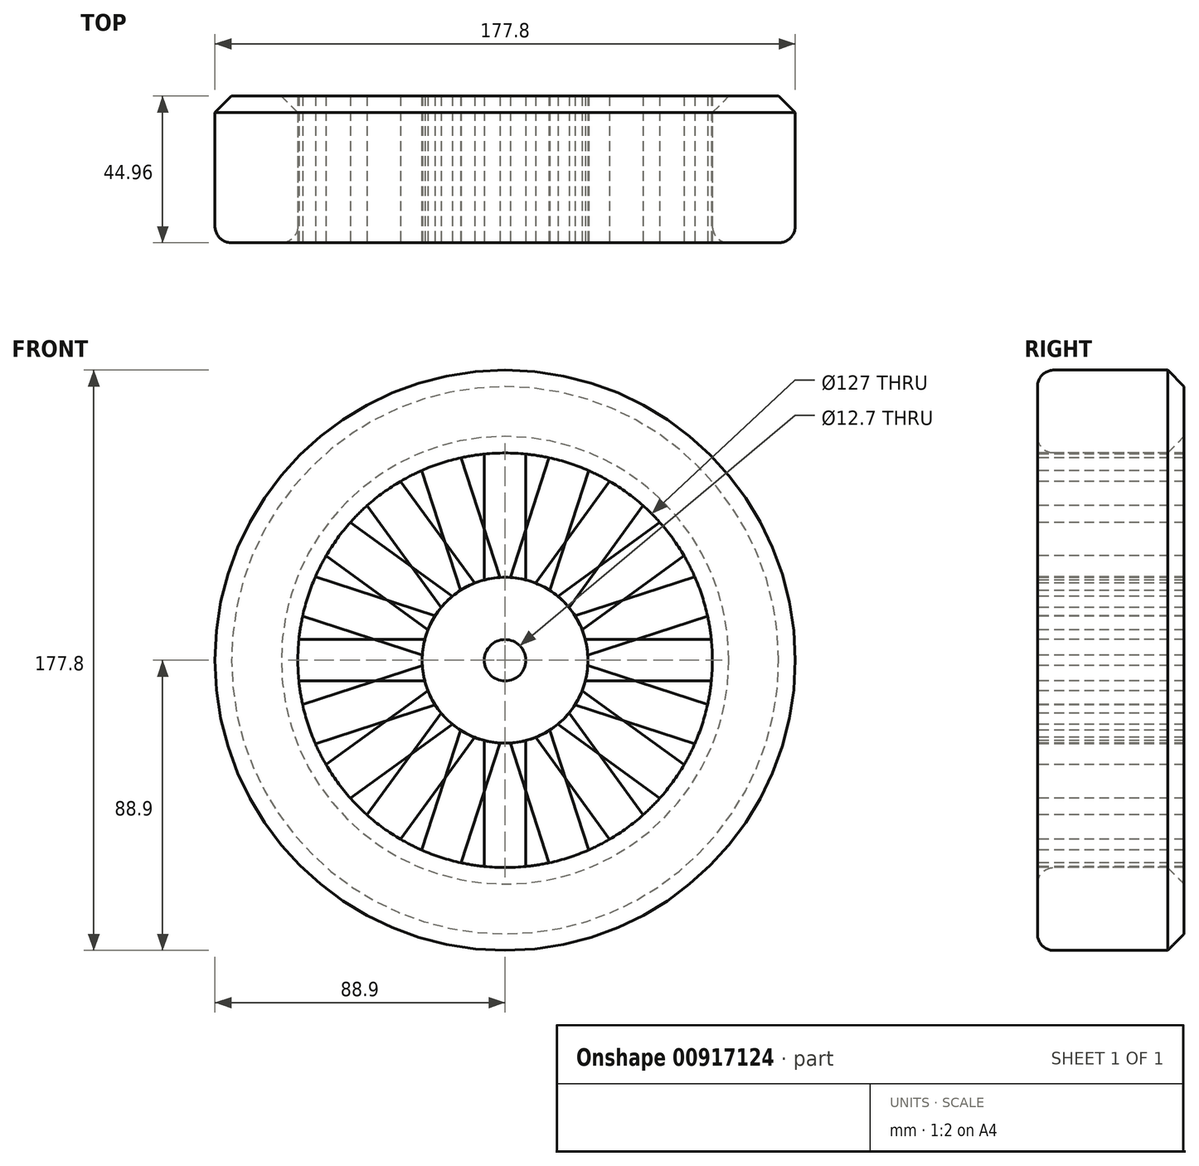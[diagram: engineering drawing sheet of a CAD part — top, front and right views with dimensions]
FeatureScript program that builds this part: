
annotation { "Feature Type Name" : "Feature", "Feature Type Description" : "" }
export const myFeature = defineFeature(function(context is Context, id is Id, definition is map)
    precondition{}
    {
        {
            var Q0;
            Q0=qCreatedBy(makeId("Front.planeOp"),FACE);
            var sketch = newSketch(context, id + "F0", { "sketchPlane" : qUnion([Q0])});
            skCircle(sketch, "E0", {"center": v(0, 0) * mm, "radius": 88.9 * mm});
            skSolve(sketch);
        }
        {
            var Q0;
            Q0=makeQuery(id+"F0.imprint","IMPRINT",FACE,{"disambiguationData":[TD([[makeQuery(id+"F0.imprint","IMPRINT",EDGE,{"derivedFrom":sQuery(id+"F0.wireOp",EDGE,"E0")}),1.0]])]});
            extrude(context, id + "F1", {"entities" : qUnion([Q0]), "depth" : 44.96 * mm, "offsetDistance" : 25.4 * mm});
        }
        {
            var Q0;
            Q0=makeQuery(id+"F1.opExtrude","CAP_FACE",FACE,{"disambiguationData":[OSD([sQuery(id+"F0.wireOp",EDGE,"E0")])],"isStart":false});
            var sketch = newSketch(context, id + "F2", { "sketchPlane" : qUnion([Q0])});
            skCircle(sketch, "E1", {"center": v(0, 0) * mm, "radius": 63.5 * mm});
            skSolve(sketch);
        }
        {
            var Q0;
            Q0=makeQuery(id+"F2.imprint","IMPRINT",FACE,{"disambiguationData":[TD([[makeQuery(id+"F2.imprint","IMPRINT",EDGE,{"derivedFrom":sQuery(id+"F2.wireOp",EDGE,"E1")}),1.0]])]});
            extrude(context, id + "F3", {"entities" : qUnion([Q0]), "operationType" : NewBodyOperationType.REMOVE, "oppositeDirection" : true, "depth" : 44.96 * mm, "offsetDistance" : 25.4 * mm});
        }
        {
            var Q0;
            Q0=makeQuery(id+"F1.opExtrude","CAP_FACE",FACE,{"disambiguationData":[OSD([sQuery(id+"F0.wireOp",EDGE,"E0")])],"isStart":false});
            var sketch = newSketch(context, id + "F4", { "sketchPlane" : qUnion([Q0])});
            skCircle(sketch, "E2", {"center": v(0, 0) * mm, "radius": 25.4 * mm});
            skSolve(sketch);
        }
        {
            var Q0;
            Q0=makeQuery(id+"F4.imprint","IMPRINT",FACE,{"disambiguationData":[TD([[makeQuery(id+"F4.imprint","IMPRINT",EDGE,{"derivedFrom":sQuery(id+"F4.wireOp",EDGE,"E2")}),1.0]])]});
            var Q1;
            Q1=makeQuery(id+"F1.opExtrude","CAP_FACE",FACE,{"disambiguationData":[OSD([sQuery(id+"F0.wireOp",EDGE,"E0")])],"isStart":true});
            extrude(context, id + "F5", {"entities" : qUnion([Q0]), "endBound" : BoundingType.UP_TO_SURFACE, "oppositeDirection" : true, "depth" : 25.4 * mm, "endBoundEntityFace" : qUnion([Q1]), "offsetDistance" : 25.4 * mm});
        }
        {
            var Q0;
            Q0=makeQuery(id+"F5.opExtrude","CAP_FACE",FACE,{"disambiguationData":[OSD([sQuery(id+"F4.wireOp",EDGE,"E2")])],"isStart":true});
            var sketch = newSketch(context, id + "F6", { "sketchPlane" : qUnion([Q0])});
            skCircle(sketch, "E3", {"center": v(0, 0) * mm, "radius": 25.4 * mm});
            skCircle(sketch, "E4", {"center": v(0, 0) * mm, "radius": 63.5 * mm});
            skLineSegment(sketch, "E5", {"start": v(6.35, 24.6) * mm, "end": v(6.35, 63.18) * mm});
            skLineSegment(sketch, "E6", {"start": v(-6.35, 24.6) * mm, "end": v(-6.35, 63.18) * mm});
            skSolve(sketch);
        }
        {
            var Q0;
            Q0=makeQuery(id+"F5.opExtrude","CAP_FACE",FACE,{"disambiguationData":[OSD([sQuery(id+"F4.wireOp",EDGE,"E2")])],"isStart":true});
            var sketch = newSketch(context, id + "F7", { "sketchPlane" : qUnion([Q0])});
            skPoint(sketch, "E7", {"position": v(0, 0) * mm});
            skSolve(sketch);
        }
        {
            var Q0;
            {var subQ0=sQuery(id+"F6.wireOp",EDGE,"E5");Q0=makeQuery(id+"F6.imprint","IMPRINT",FACE,{"disambiguationData":[TD([[makeQuery(id+"F6.imprint","IMPRINT",EDGE,{"derivedFrom":subQ0}),1.0]])]});}
            var Q1;
            Q1=makeQuery(id+"F1.opExtrude","CAP_FACE",FACE,{"disambiguationData":[OSD([sQuery(id+"F0.wireOp",EDGE,"E0")])],"isStart":true});
            extrude(context, id + "F8", {"entities" : qUnion([Q0]), "endBound" : BoundingType.UP_TO_SURFACE, "oppositeDirection" : true, "depth" : 25.4 * mm, "endBoundEntityFace" : qUnion([Q1]), "offsetDistance" : 25.4 * mm});
        }
        {
            var Q0;
            Q0=makeQuery(id+"F8.opExtrude","SWEPT_BODY",BODY,{"disambiguationData":[OSD([sQuery(id+"F6.wireOp",EDGE,"E3"),sQuery(id+"F6.wireOp",EDGE,"E4"),sQuery(id+"F6.wireOp",EDGE,"E5"),sQuery(id+"F6.wireOp",EDGE,"E6")])]});
            var Q1;
            Q1=makeQuery(id+"F1.opExtrude","SWEPT_FACE",FACE,{"disambiguationData":[OSD([sQuery(id+"F0.wireOp",EDGE,"E0")])]});
            circularPattern(context, id + "F9", {"entities" : qUnion([Q0]), "axis" : qUnion([Q1]), "angle" : 360 * degree, "instanceCount" : 20, "oppositeDirection" : true, "equalSpace" : true});
        }
        {
            var Q0;
            Q0=sQuery(id+"F7.wireOp",VERTEX,"E7");
            var Q1;
            Q1=makeQuery(id+"F5.opExtrude","SWEPT_BODY",BODY,{"disambiguationData":[OSD([sQuery(id+"F4.wireOp",EDGE,"E2")])]});
            hole(context, id + "F10", {"style" : HoleStyle.C_BORE, "endStyle" : HoleEndStyle.THROUGH, "holeDiameter" : 12.7 * mm, "cBoreDiameter" : 12.7 * mm, "cBoreDepth" : 6.35 * mm, "majorDiameter" : 6.35 * mm, "isTappedThrough" : true, "tappedDepth" : 12.7 * mm, "tapClearance" : 3, "locations" : qUnion([Q0]), "scope" : qUnion([Q1])});
        }
        {
            var Q0;
            Q0=makeQuery(id+"F1.opExtrude","CAP_FACE",FACE,{"disambiguationData":[OSD([sQuery(id+"F0.wireOp",EDGE,"E0")])],"isStart":false});
            fillet(context, id + "F11", {"entities" : qUnion([Q0]), "radius" : 5.08 * mm, "tangentPropagation" : true, "allowEdgeOverflow" : false});
        }
        {
            var Q0;
            Q0=makeQuery(id+"F1.opExtrude","CAP_FACE",FACE,{"disambiguationData":[OSD([sQuery(id+"F0.wireOp",EDGE,"E0")])],"isStart":true});
            chamfer(context, id + "F12", {"entities" : qUnion([Q0]), "width" : 5.08 * mm, "tangentPropagation" : true});
        }
    });
